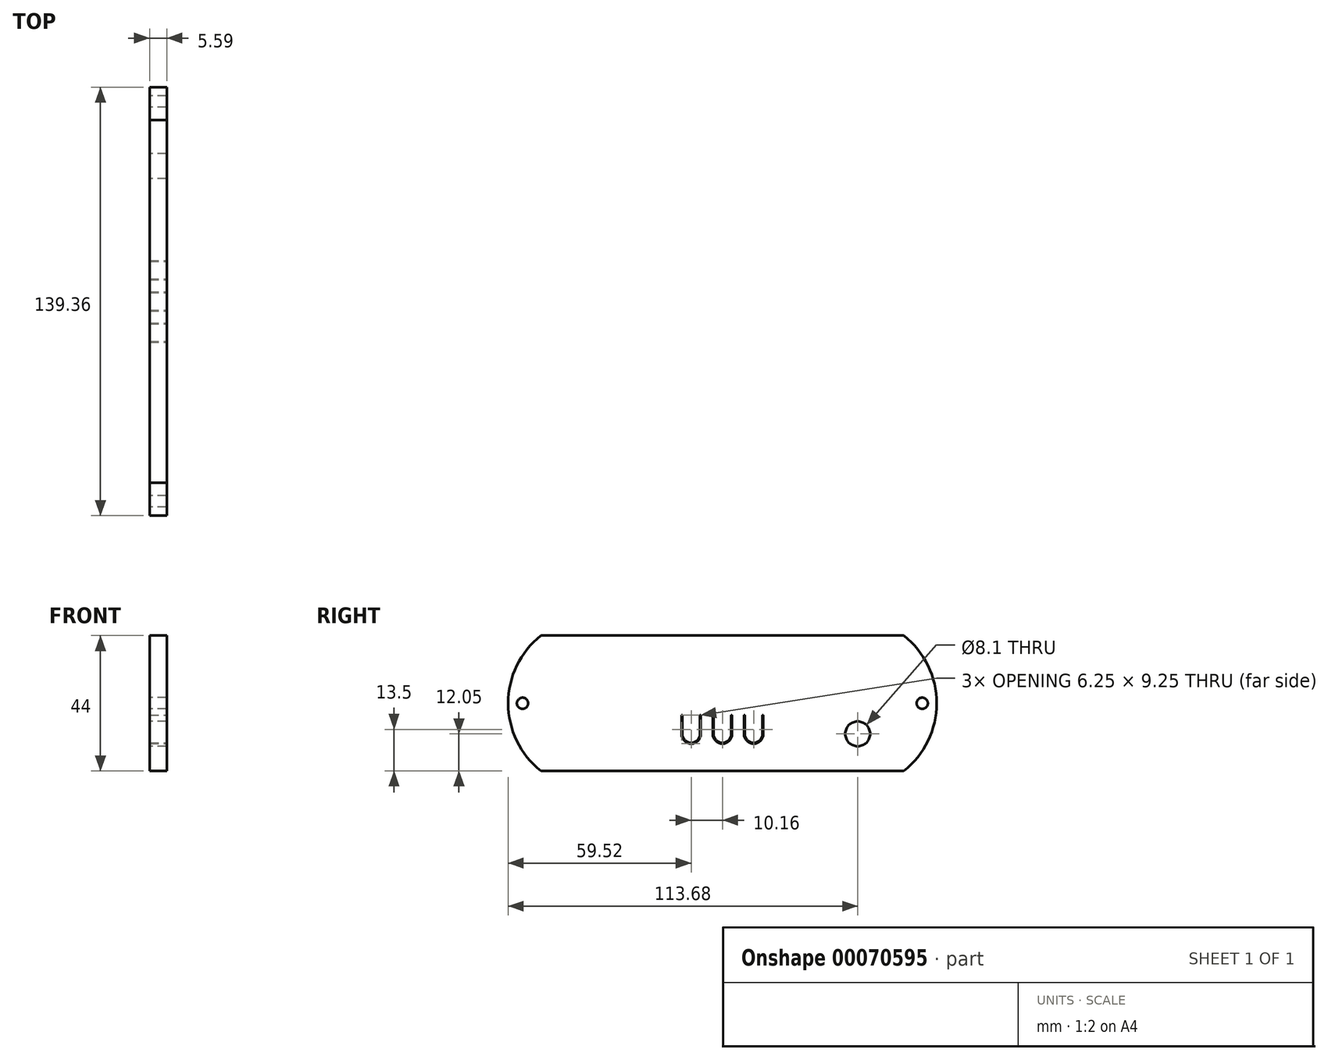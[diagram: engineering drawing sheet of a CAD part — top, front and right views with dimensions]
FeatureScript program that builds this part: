
annotation { "Feature Type Name" : "Feature", "Feature Type Description" : "" }
export const myFeature = defineFeature(function(context is Context, id is Id, definition is map)
    precondition{}
    {
        {
            var Q0;
            Q0=qCreatedBy(makeId("Right.planeOp"),FACE);
            var sketch = newSketch(context, id + "F0", { "sketchPlane" : qUnion([Q0])});
            skLineSegment(sketch, "E0.rect.bottom", {"start": v(59, 22) * mm, "end": v(-59, 22) * mm});
            skLineSegment(sketch, "E0.rect.top", {"start": v(59, -22) * mm, "end": v(-59, -22) * mm});
            skLineSegment(sketch, "E0.rect.left", {"start": v(59, 22) * mm, "end": v(59, -22) * mm, "construction": true});
            skLineSegment(sketch, "E0.rect.right", {"start": v(-59, 22) * mm, "end": v(-59, -22) * mm, "construction": true});
            skPoint(sketch, "E0.rect.middle", {"position": v(0, 0) * mm});
            skLineSegment(sketch, "E1", {"start": v(-59, 0) * mm, "end": v(59, 0) * mm, "construction": true});
            skArc(sketch, "E2", {"start": v(-59, 22) * mm, "mid": v(-69.68, 0) * mm, "end": v(-59, -22) * mm});
            skArc(sketch, "E3", {"start": v(59, -22) * mm, "mid": v(69.68, 0) * mm, "end": v(59, 22) * mm});
            skCircle(sketch, "E4", {"center": v(-65, 0) * mm, "radius": 1.83 * mm});
            skCircle(sketch, "E5", {"center": v(65, 0) * mm, "radius": 1.83 * mm});
            skCircle(sketch, "E6", {"center": v(44, -9.95) * mm, "radius": 4.05 * mm});
            skSolve(sketch);
        }
        {
            var Q0;
            Q0=makeQuery(id+"F0.imprint","IMPRINT",FACE,{"disambiguationData":[TD([[makeQuery(id+"F0.imprint","IMPRINT",EDGE,{"derivedFrom":sQuery(id+"F0.wireOp",EDGE,"E0.rect.bottom")}),1.0]])]});
            extrude(context, id + "F1", {"entities" : qUnion([Q0]), "depth" : 5.6 * mm});
        }
        {
            var Q0;
            Q0=makeQuery(id+"F1.opExtrude","CAP_FACE",FACE,{"disambiguationData":[OSD([sQuery(id+"F0.wireOp",EDGE,"E0.rect.bottom"),sQuery(id+"F0.wireOp",EDGE,"E0.rect.top"),sQuery(id+"F0.wireOp",EDGE,"E2"),sQuery(id+"F0.wireOp",EDGE,"E3"),sQuery(id+"F0.wireOp",EDGE,"E4"),sQuery(id+"F0.wireOp",EDGE,"E5"),sQuery(id+"F0.wireOp",EDGE,"E6")])],"isStart":false});
            var sketch = newSketch(context, id + "F2", { "sketchPlane" : qUnion([Q0])});
            skLineSegment(sketch, "E7", {"start": v(7.16, -4) * mm, "end": v(7.16, -10) * mm, "construction": true});
            skArc(sketch, "E8", {"start": v(7.16, -10) * mm, "mid": v(10.16, -13) * mm, "end": v(13.16, -10) * mm, "construction": true});
            skLineSegment(sketch, "E9", {"start": v(13.16, -10) * mm, "end": v(13.16, -4) * mm, "construction": true});
            skArc(sketch, "E10.0.startCap", {"start": v(7.03, -4) * mm, "mid": v(7.16, -3.87) * mm, "end": v(7.29, -4) * mm});
            skLineSegment(sketch, "E10.0.left", {"start": v(7.29, -4) * mm, "end": v(7.29, -10) * mm});
            skLineSegment(sketch, "E10.0.right", {"start": v(7.03, -4) * mm, "end": v(7.03, -10) * mm});
            skArc(sketch, "E10.1.left", {"start": v(7.29, -10) * mm, "mid": v(10.16, -12.87) * mm, "end": v(13.03, -10) * mm});
            skArc(sketch, "E10.1.right", {"start": v(7.03, -10) * mm, "mid": v(10.16, -13.13) * mm, "end": v(13.29, -10) * mm});
            skArc(sketch, "E10.2.endCap", {"start": v(13.03, -4) * mm, "mid": v(13.16, -3.87) * mm, "end": v(13.29, -4) * mm});
            skLineSegment(sketch, "E10.2.left", {"start": v(13.03, -10) * mm, "end": v(13.03, -4) * mm});
            skLineSegment(sketch, "E10.2.right", {"start": v(13.29, -10) * mm, "end": v(13.29, -4) * mm});
            skArc(sketch, "E11.1.0.0", {"start": v(-2.87, -10) * mm, "mid": v(0, -12.87) * mm, "end": v(2.87, -10) * mm});
            skLineSegment(sketch, "E11.1.0.1", {"start": v(3.13, -10) * mm, "end": v(3.13, -4) * mm});
            skLineSegment(sketch, "E11.1.0.2", {"start": v(2.87, -10) * mm, "end": v(2.87, -4) * mm});
            skArc(sketch, "E11.1.0.3", {"start": v(-3.13, -10) * mm, "mid": v(0, -13.13) * mm, "end": v(3.13, -10) * mm});
            skLineSegment(sketch, "E11.1.0.4", {"start": v(-2.87, -4) * mm, "end": v(-2.87, -10) * mm});
            skLineSegment(sketch, "E11.1.0.5", {"start": v(-3.13, -4) * mm, "end": v(-3.13, -10) * mm});
            skArc(sketch, "E11.1.0.6", {"start": v(-3.13, -4) * mm, "mid": v(-3, -3.87) * mm, "end": v(-2.87, -4) * mm});
            skArc(sketch, "E11.1.0.7", {"start": v(2.87, -4) * mm, "mid": v(3, -3.87) * mm, "end": v(3.13, -4) * mm});
            skArc(sketch, "E11.2.0.0", {"start": v(-13.03, -10) * mm, "mid": v(-10.16, -12.87) * mm, "end": v(-7.29, -10) * mm});
            skLineSegment(sketch, "E11.2.0.1", {"start": v(-7.03, -10) * mm, "end": v(-7.03, -4) * mm});
            skLineSegment(sketch, "E11.2.0.2", {"start": v(-7.29, -10) * mm, "end": v(-7.29, -4) * mm});
            skArc(sketch, "E11.2.0.3", {"start": v(-13.29, -10) * mm, "mid": v(-10.16, -13.13) * mm, "end": v(-7.03, -10) * mm});
            skLineSegment(sketch, "E11.2.0.4", {"start": v(-13.03, -4) * mm, "end": v(-13.03, -10) * mm});
            skLineSegment(sketch, "E11.2.0.5", {"start": v(-13.29, -4) * mm, "end": v(-13.29, -10) * mm});
            skArc(sketch, "E11.2.0.6", {"start": v(-13.29, -4) * mm, "mid": v(-13.16, -3.87) * mm, "end": v(-13.03, -4) * mm});
            skArc(sketch, "E11.2.0.7", {"start": v(-7.29, -4) * mm, "mid": v(-7.16, -3.87) * mm, "end": v(-7.03, -4) * mm});
            skLineSegment(sketch, "E11.direction1", {"start": v(7.03, -10) * mm, "end": v(-3.13, -10) * mm, "construction": true});
            skSolve(sketch);
        }
        {
            var Q0;
            Q0 = qSketchRegion(id + "F2", true);
            extrude(context, id + "F3", {"entities" : qUnion([Q0]), "operationType" : NewBodyOperationType.REMOVE, "endBound" : BoundingType.UP_TO_NEXT, "oppositeDirection" : true, "depth" : 25 * mm});
        }
    });
